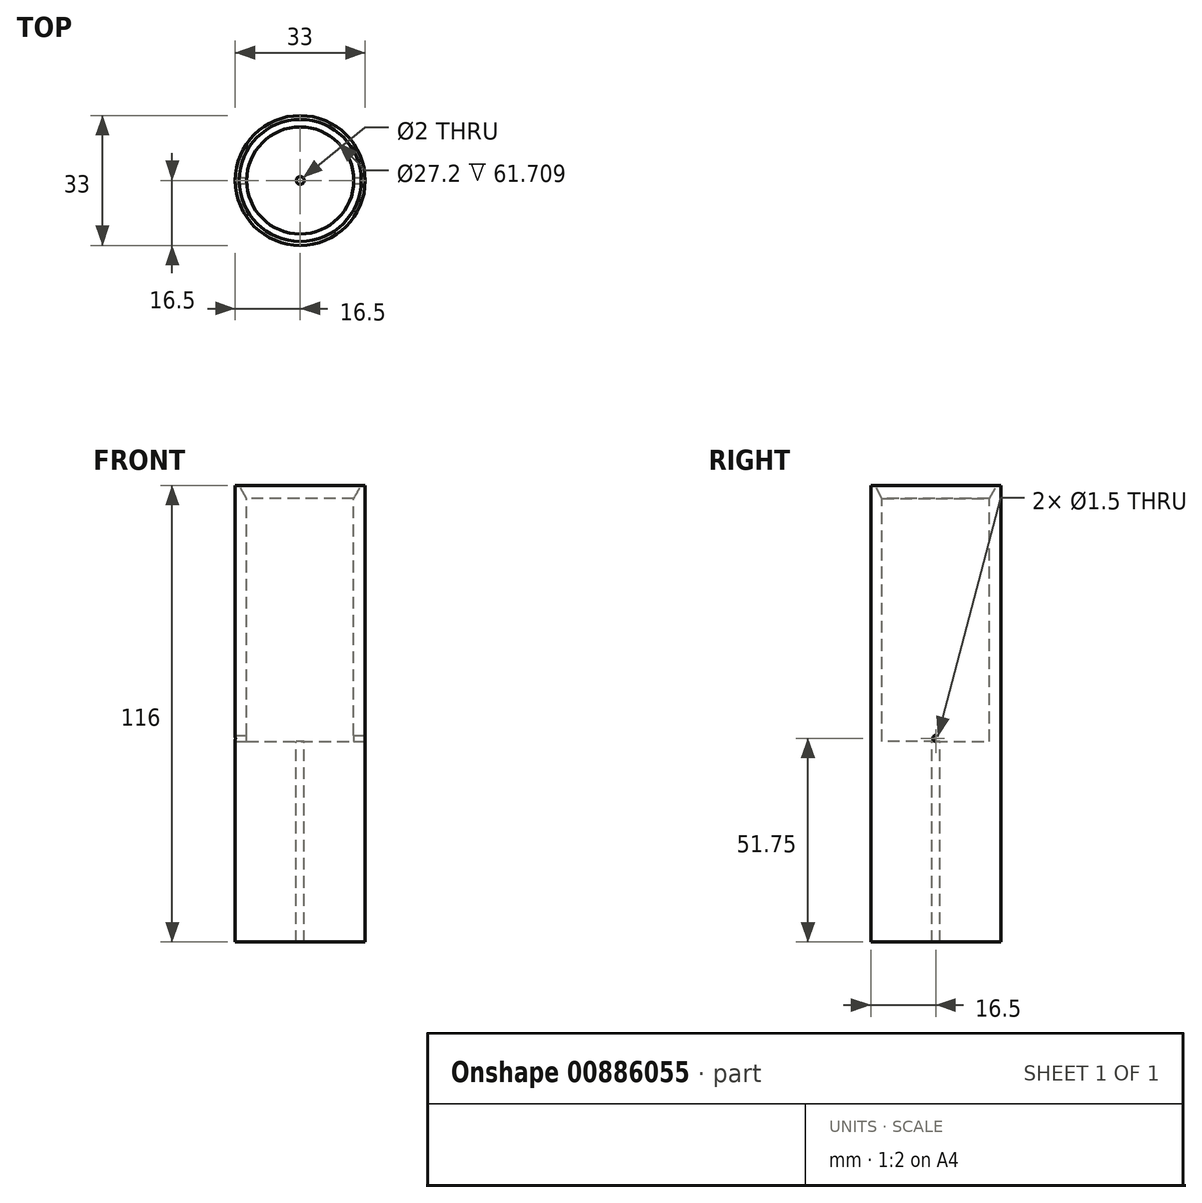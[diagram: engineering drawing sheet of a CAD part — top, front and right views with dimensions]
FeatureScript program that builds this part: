
annotation { "Feature Type Name" : "Feature", "Feature Type Description" : "" }
export const myFeature = defineFeature(function(context is Context, id is Id, definition is map)
    precondition{}
    {
        {
            var Q0;
            Q0=qCreatedBy(makeId("Top.planeOp"),FACE);
            var sketch = newSketch(context, id + "F0", { "sketchPlane" : qUnion([Q0])});
            skCircle(sketch, "E0", {"center": v(0, 0) * mm, "radius": 16.5 * mm});
            skSolve(sketch);
        }
        {
            var Q0;
            Q0 = qSketchRegion(id + "F0", true);
            extrude(context, id + "F1", {"entities" : qUnion([Q0]), "depth" : 116 * mm, "offsetDistance" : 25 * mm, "symmetric" : true});
        }
        {
            var Q0;
            Q0=qCreatedBy(makeId("Front.planeOp"),FACE);
            var sketch = newSketch(context, id + "F2", { "sketchPlane" : qUnion([Q0])});
            skLineSegment(sketch, "E1", {"start": v(0, -59.3) * mm, "end": v(0, 69.95) * mm});
            skLineSegment(sketch, "E2", {"start": v(0, 69.95) * mm, "end": v(-22.4, 69.95) * mm});
            skLineSegment(sketch, "E3", {"start": v(-22.4, 69.95) * mm, "end": v(-13.6, 54.7) * mm});
            skLineSegment(sketch, "E4", {"start": v(-13.6, 54.7) * mm, "end": v(-13.6, -7) * mm});
            skLineSegment(sketch, "E5", {"start": v(-13.6, -7) * mm, "end": v(-1, -7) * mm});
            skLineSegment(sketch, "E6", {"start": v(-1, -7) * mm, "end": v(-1, -58.22) * mm});
            skLineSegment(sketch, "E7", {"start": v(-1, -58.22) * mm, "end": v(-14.5, -58.22) * mm});
            skLineSegment(sketch, "E8", {"start": v(-14.5, -58.22) * mm, "end": v(-14.5, -59.3) * mm});
            skLineSegment(sketch, "E9", {"start": v(-14.5, -59.3) * mm, "end": v(0, -59.3) * mm});
            skPoint(sketch, "E10", {"position": v(-15.5, 58) * mm});
            skLineSegment(sketch, "E11.0.0", {"start": v(-16.5, 58) * mm, "end": v(16.5, 58) * mm, "construction": true});
            skLineSegment(sketch, "E12.0.0", {"start": v(16.5, -58) * mm, "end": v(-16.5, -58) * mm, "construction": true});
            skSolve(sketch);
        }
        {
            var Q0;
            Q0 = qSketchRegion(id + "F2", true);
            var Q1;
            Q1=sQuery(id+"F2.wireOp",EDGE,"E1");
            revolve(context, id + "F3", {"operationType" : NewBodyOperationType.REMOVE, "surfaceOperationType" : NewSurfaceOperationType.NEW, "entities" : qUnion([Q0]), "axis" : qUnion([Q1]), "revolveType" : RevolveType.FULL, "oppositeDirection" : true});
        }
        {
            var Q0;
            Q0=qCreatedBy(makeId("Right.planeOp"),FACE);
            var sketch = newSketch(context, id + "F4", { "sketchPlane" : qUnion([Q0])});
            skCircle(sketch, "E13", {"center": v(0, -6.25) * mm, "radius": 0.75 * mm});
            skSolve(sketch);
        }
        {
            var Q0;
            Q0 = qSketchRegion(id + "F4", true);
            extrude(context, id + "F5", {"entities" : qUnion([Q0]), "operationType" : NewBodyOperationType.REMOVE, "oppositeDirection" : true, "depth" : 40 * mm, "offsetDistance" : 25 * mm, "symmetric" : true});
        }
    });
